# Revit family: Toilet_Seat-Elongated_Closed_Front-Cleansing-KOHLER-C3-150-K-8297T_1
name_source: partatom
category: Plumbing Fixtures
revit_build: Autodesk Revit 2017 (Build: 20160225_1515(x64)
units: mm (PartAtom-declared; Revit-internal decimal feet)

## family parameters
Cut with Voids When Loaded = No
Host = Face
OmniClass Number = 23.31.19.19.17
OmniClass Title = Water Closet Seats
Part Type = Normal
Room Calculation Point = No
Round Connector Dimension = Use Diameter
Shared = No

## types (2) — shared parameters
ADA Compliant = No
Apparent Load = 2200 VA
Assembly Code = C1030200
CW Connection = Yes
Cold Water Inlet = Cold Water Inlet
Date Modified = 06/24/2021
Default Elevation = 0"
Electrical Connector = Yes
Electrical Note = Ground-Fault Circuit-Interrupter
Finish = Kohler-Plastic-0-White
Flow Rate = 0 GPM
HW Connection = No
Height = 5 3/4"
Hot Water Inlet = Hot Water Inlet
Length = 20 11/16"
Manufacturer = KOHLER Co.
Master Format 2014 = 10 28 00
Master Format 2014 Name = Toilet, Bath, and Laundry Accessories
Material = Plastic
Pressure = 0.00 psi
Product Documentation Link = https://files.kohler.com.cn
Product Name = C3-150
Product Page URL = https://www.kohler.com.cn
URL = http://www.kohler.com.cn
Vent Connection = No
Voltage = 220 V
Waste Connection = No
Waste Water Outlet = Waste Water Outlet
WaterSense Certified = Yes
Width = 17 5/8"

## per-type parameters (varying)
| type | Description | Model | Type |
| Hidden Chord, 0-White | Qingshubao Smart Toilet Cover (Combined Version) | K-8297T-HC-0 | 1 |
| Cloud Version, 0-White | Qingshubao Smart Cover (Cloud Smart Version) | K-8297T-XP-0 | 2 |

## geometry (parser evidence)
native form markers: Sweep x4
no freeform markers — native parametric forms only
